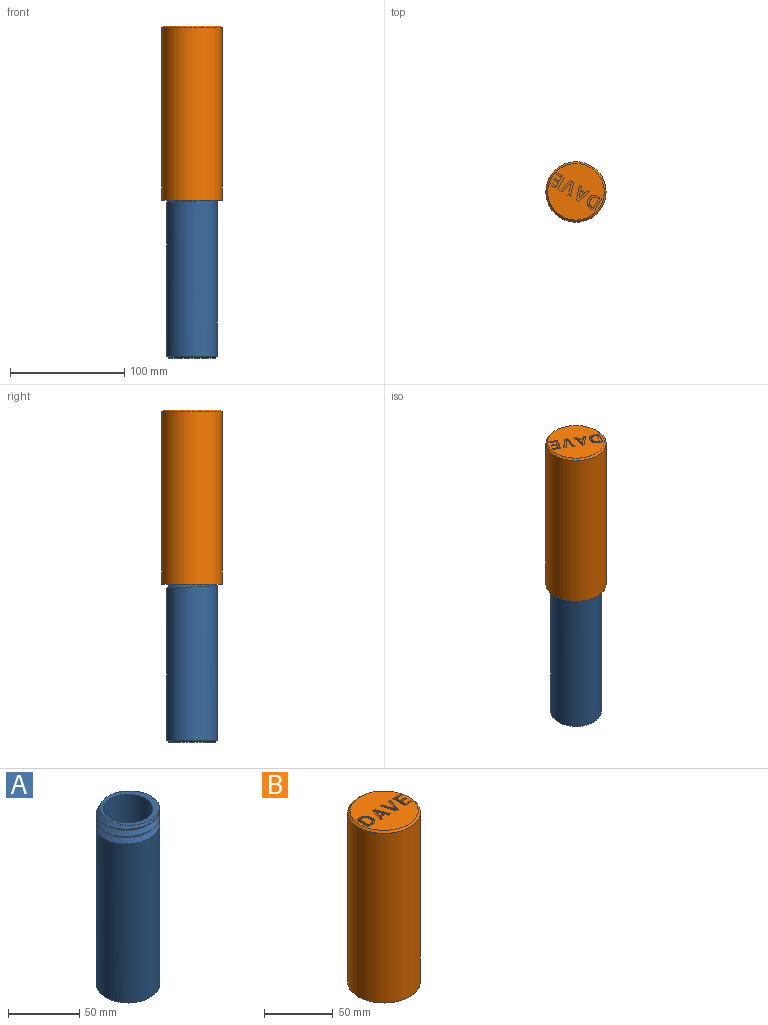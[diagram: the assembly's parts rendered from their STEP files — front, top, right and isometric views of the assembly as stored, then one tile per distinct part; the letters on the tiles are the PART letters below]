
ASSEMBLY  parts=2 mates=1
PART A: 11 faces, bbox 47.1x54x158.5 mm
  f0: cylinder r=22.23mm len=138.58mm, axis (0,0,-1), area 18908.5mm2, adj f1,f7,f8,f10
  f1: cylinder r=22.23mm len=44.45mm, axis (0,0,-1), area 65.2mm2, adj f0,f2,f9,f10
  f2: cylinder r=22.23mm len=44.45mm, axis (0,0,-1), area 63.2mm2, adj f1,f3,f9,f10
  f3: plane 44.26x44.22mm, normal (0,0,1), area 398.2mm2, adj f2,f5,f9,f10
  f4: plane 41.28x41.28mm, normal (0,0,-1), area 1338mm2, adj f7
  f5: cylinder r=17.46mm len=147.64mm, axis (0,0,-1), area 16198.8mm2, adj f3,f6
  f6: plane 34.93x34.93mm, normal (0,0,1), area 958mm2, adj f5
  f7: cone r=22.23mm half-angle=45deg, axis (0,0,1), area 302.3mm2, adj f0,f4
  f8: plane 5.88x3.18mm, normal (0,1,0), area 9.3mm2, adj f0,f9,f10
  f9: bspline ~51.33x44.45mm, area 1248.9mm2, adj f1,f2,f3,f8,f10
  f10: bspline ~51.33x44.45mm, area 1515.8mm2, adj f0,f1,f2,f3,f8,f9
PART B: 85 faces, bbox 54.9x54.9x158 mm
  f0: plane 49.53x49.53mm, normal (0,0,1), area 1725.7mm2, adj f11,f12,f13,f14,f15,f16,f18,f19
  f1: cylinder r=26.35mm len=150.81mm, axis (0,0,1), area 24971.2mm2, adj f2,f11
  f2: plane 54.92x54.92mm, normal (0,0,-1), area 786.2mm2, adj f1,f3,f6,f9,f10
  f3: cylinder r=19.62mm len=39.24mm, axis (0,0,1), area 65.5mm2, adj f2,f4,f6,f9,f10
  f4: cylinder r=19.62mm len=39.24mm, axis (0,0,1), area 67.9mm2, adj f3,f5,f9,f10
  f5: cylinder r=19.62mm len=133.49mm, axis (0,0,1), area 16065.3mm2, adj f4,f7,f8,f10
  f6: cylinder r=19.62mm len=0.75mm, axis (0,0,1), area 0mm2, adj f2,f3,f9
  f7: plane 39.24x39.24mm, normal (0,0,-1), area 1209.5mm2, adj f5
  f8: plane 5.8x3.14mm, normal (0,-1,0), area 9.1mm2, adj f5,f9,f10
  f9: bspline ~52.56x45.52mm, area 1274.4mm2, adj f2,f3,f4,f6,f8,f10
  f10: bspline ~52.56x45.52mm, area 1526.8mm2, adj f2,f3,f4,f5,f8,f9
  f11: cone r=24.77mm half-angle=45deg, axis (0,0,-1), area 360.5mm2, adj f0,f1
  f12: plane 2.27x1.59mm, normal (0,-1,0), area 3.6mm2, adj f0,f13,f16,f17
  f13: plane 12.28x3.79mm, normal (0.96,0.3,0), area 20.4mm2, adj f0,f12,f14,f17
  f14: plane 1.59x1.04mm, normal (0,1,0), area 1.7mm2, adj f0,f13,f15,f17
  f15: plane 2.7x1.59mm, normal (-1,0,0), area 4.3mm2, adj f0,f14,f16,f17
  f16: plane 9.58x2.57mm, normal (-0.97,-0.26,0), area 15.7mm2, adj f0,f12,f15,f17
  f17: plane 12.28x4.84mm, normal (0,0,1), area 23.8mm2, adj f12,f13,f14,f15,f16
  f18: plane 1.59x1.34mm, normal (-0.94,-0.34,0), area 2.3mm2, adj f0,f19,f21,f22
  f19: plane 2.22x1.59mm, normal (0,-1,0), area 3.5mm2, adj f0,f18,f20,f22
  f20: plane 1.59x1.34mm, normal (0.95,-0.33,0), area 2.3mm2, adj f0,f19,f21,f22
  f21: plane 3.17x1.59mm, normal (0,1,0), area 5mm2, adj f0,f18,f20,f22
  f22: plane 3.17x1.34mm, normal (0,0,1), area 3.6mm2, adj f18,f19,f20,f21
  f23: plane 2.05x1.59mm, normal (0,1,0), area 3.3mm2, adj f0,f24,f29,f30
  f24: plane 12.2x4.24mm, normal (-0.94,-0.33,0), area 20.5mm2, adj f0,f23,f25,f30
  f25: plane 1.97x1.59mm, normal (0,-1,0), area 3.1mm2, adj f0,f24,f26,f30
  f26: plane 12.2x4.27mm, normal (0.94,-0.33,0), area 20.5mm2, adj f0,f25,f27,f30
  f27: plane 2.07x1.59mm, normal (0,1,0), area 3.3mm2, adj f0,f26,f28,f30
  f28: plane 9.15x3.2mm, normal (-0.94,0.33,0), area 15.4mm2, adj f0,f27,f29,f30
  f29: plane 9.15x3.17mm, normal (0.95,0.33,0), area 15.4mm2, adj f0,f23,f28,f30
  f30: plane 12.2x10.49mm, normal (0,0,1), area 46.9mm2, adj f23,f24,f25,f26,f27,f28,f29
  f31: extruded ~2.71x1.59mm, area 4.4mm2, adj f0,f32,f52,f53
  f32: plane 1.59x1.01mm, normal (0,-1,0), area 1.6mm2, adj f0,f31,f33,f53
  f33: plane 1.59x1.51mm, normal (1,0,0), area 2.4mm2, adj f0,f32,f34,f53
  f34: plane 1.59x0.48mm, normal (0,1,0), area 0.8mm2, adj f0,f33,f35,f53
  f35: extruded ~2.32x1.59mm, area 3.8mm2, adj f0,f34,f36,f53
  f36: extruded ~1.59x1.42mm, area 2.8mm2, adj f0,f35,f37,f53
  f37: extruded ~1.59x1.35mm, area 2.4mm2, adj f0,f36,f38,f53
  f38: extruded ~1.59x1.51mm, area 2.4mm2, adj f0,f37,f39,f53
  f39: extruded ~3.75x1.59mm, area 6.2mm2, adj f0,f38,f40,f53
  f40: extruded ~2.92x1.59mm, area 5.3mm2, adj f0,f39,f41,f53
  f41: plane 1.59x1.29mm, normal (0,-1,0), area 2.1mm2, adj f0,f40,f42,f53
  f42: plane 1.59x1.46mm, normal (1,0,0), area 2.3mm2, adj f0,f41,f43,f53
  f43: plane 1.96x1.59mm, normal (0,1,0), area 3.1mm2, adj f0,f42,f44,f53
  f44: extruded ~1.59x0.71mm, area 1.1mm2, adj f0,f43,f45,f53
  f45: extruded ~1.59x1.06mm, area 1.7mm2, adj f0,f44,f46,f53
  f46: extruded ~1.59x1.2mm, area 2.2mm2, adj f0,f45,f47,f53
  f47: extruded ~1.59x1.13mm, area 2.5mm2, adj f0,f46,f48,f53
  f48: extruded ~1.79x1.59mm, area 3.1mm2, adj f0,f47,f49,f53
  f49: extruded ~2.58x1.59mm, area 4.1mm2, adj f0,f48,f50,f53
  f50: extruded ~2.13x1.59mm, area 3.5mm2, adj f0,f49,f51,f53
  f51: extruded ~1.85x1.59mm, area 3.5mm2, adj f0,f50,f52,f53
  f52: extruded ~1.94x1.59mm, area 3.7mm2, adj f0,f31,f51,f53
  f53: plane 12.21x7.19mm, normal (0,0,1), area 33.6mm2, adj f31,f32,f33,f34,f35,f36,f37,f38
  f54: plane 2.25x1.59mm, normal (0,-1,0), area 3.6mm2, adj f0,f55,f58,f59
  f55: plane 9.05x2.59mm, normal (0.96,-0.27,0), area 14.9mm2, adj f0,f54,f56,f59
  f56: plane 3.23x1.59mm, normal (1,0,0), area 5.1mm2, adj f0,f55,f57,f59
  f57: plane 1.59x0.86mm, normal (0,1,0), area 1.4mm2, adj f0,f56,f58,f59
  f58: plane 12.28x3.98mm, normal (-0.95,0.31,0), area 20.5mm2, adj f0,f54,f57,f59
  f59: plane 12.28x4.84mm, normal (0,0,1), area 23.3mm2, adj f54,f55,f56,f57,f58
  f60: plane 2.02x1.59mm, normal (0,-1,0), area 3.2mm2, adj f0,f61,f63,f64
  f61: plane 12.21x1.59mm, normal (1,0,0), area 19.4mm2, adj f0,f60,f62,f64
  f62: plane 2.02x1.59mm, normal (0,1,0), area 3.2mm2, adj f0,f61,f63,f64
  f63: plane 12.21x1.59mm, normal (-1,0,0), area 19.4mm2, adj f0,f60,f62,f64
  f64: plane 12.21x2.02mm, normal (0,0,1), area 24.7mm2, adj f60,f61,f62,f63
  f65: plane 4.42x1.59mm, normal (0,1,0), area 7mm2, adj f0,f66,f68,f69
  f66: plane 1.59x1.36mm, normal (-1,0,0), area 2.2mm2, adj f0,f65,f67,f69
  f67: plane 4.42x1.59mm, normal (0,-1,0), area 7mm2, adj f0,f66,f68,f69
  f68: plane 1.59x1.36mm, normal (1,0,0), area 2.2mm2, adj f0,f65,f67,f69
  f69: plane 4.42x1.36mm, normal (0,0,1), area 6mm2, adj f65,f66,f67,f68
  f70: plane 4.94x1.59mm, normal (0,-1,0), area 7.8mm2, adj f0,f71,f73,f74
  f71: plane 1.59x1.51mm, normal (1,0,0), area 2.4mm2, adj f0,f70,f72,f74
  f72: plane 4.94x1.59mm, normal (0,1,0), area 7.8mm2, adj f0,f71,f73,f74
  f73: plane 1.59x1.51mm, normal (-1,0,0), area 2.4mm2, adj f0,f70,f72,f74
  f74: plane 4.94x1.51mm, normal (0,0,1), area 7.4mm2, adj f70,f71,f72,f73
  f75: plane 1.59x1.51mm, normal (-1,0,0), area 2.4mm2, adj f0,f76,f78,f79
  f76: plane 4.94x1.59mm, normal (0,-1,0), area 7.8mm2, adj f0,f75,f77,f79
  f77: plane 1.59x1.51mm, normal (1,0,0), area 2.4mm2, adj f0,f76,f78,f79
  f78: plane 4.94x1.59mm, normal (0,1,0), area 7.8mm2, adj f0,f75,f77,f79
  f79: plane 4.94x1.51mm, normal (0,0,1), area 7.4mm2, adj f75,f76,f77,f78
  f80: plane 1.99x1.59mm, normal (0,-1,0), area 3.2mm2, adj f0,f81,f83,f84
  f81: plane 12.21x1.59mm, normal (1,0,0), area 19.4mm2, adj f0,f80,f82,f84
  f82: plane 1.99x1.59mm, normal (0,1,0), area 3.2mm2, adj f0,f81,f83,f84
  f83: plane 12.21x1.59mm, normal (-1,0,0), area 19.4mm2, adj f0,f80,f82,f84
  f84: plane 12.21x1.99mm, normal (0,0,1), area 24.3mm2, adj f80,f81,f82,f83
PLACE A rot(axis=(0,0,1),67.2deg) t=(115.16,-38.74,-172.89)mm
PLACE B rot(axis=(0,0,1),149.7deg) t=(115.16,-38.74,117.87)mm
MATE cylindrical A.f0 <-> B.f1  axis (0,0,1) through (115.16,-38.74,-20.49)mm
